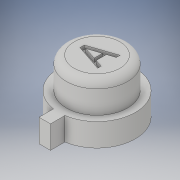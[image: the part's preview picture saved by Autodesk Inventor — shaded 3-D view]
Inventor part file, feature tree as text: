
AUTODESK INVENTOR PART (.ipt)
format: ipt  version: 2019 (Build 230136000, 136)  size: 154,112 bytes
history: native  units: mm
features: extrude x2, sketch x2, revolve x1
ambient origin geometry x8: Origin, YZ Plane, XZ Plane, XY Plane, X Axis, Y Axis, Z Axis, Center Point
bodies: Volumenkörper1 (feature_tree)
feature tree (5):
  revolve  "Umdrehung1"
  extrude  "Extrusion1"  Depth=4.0mm
  extrude  "Extrusion3"  Depth=5.0mm
  sketch  "Skizze2"  dims[d0=2.0mm d1=4.0mm]
  sketch  "Skizze4"  dims[d2=3.0mm d3=5.0mm d4=3.0mm d5=1.0mm d6=1.0mm d7=90.0deg d8=0.5mm d9=0.0mm d15=1.5mm d16=2.0mm d17=3.0mm d18=0.0mm d19=0.75mm]
